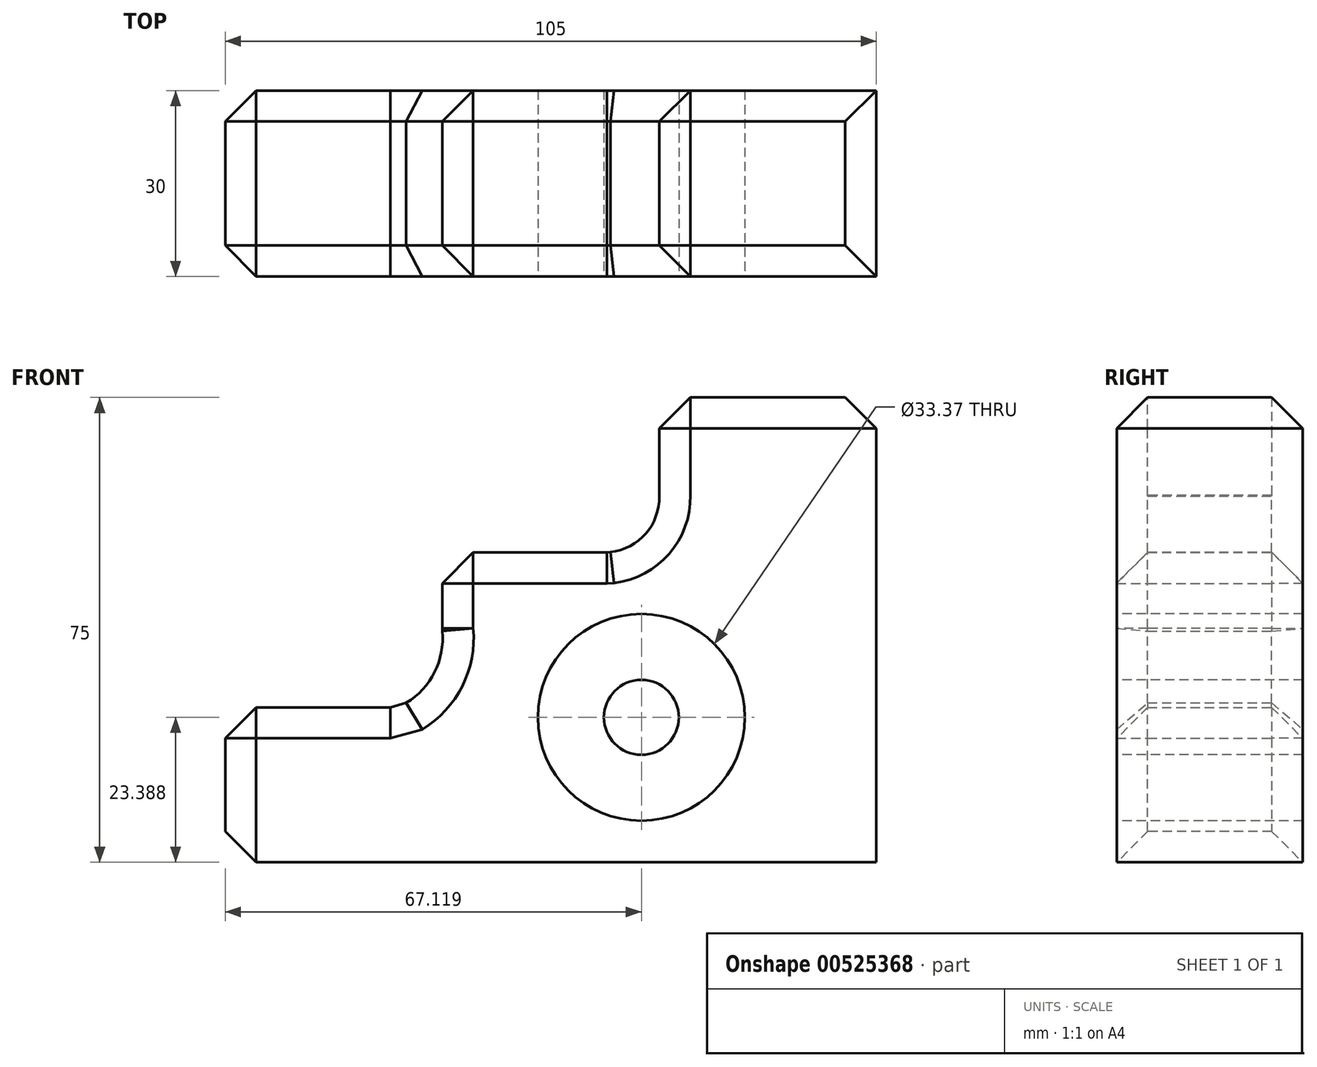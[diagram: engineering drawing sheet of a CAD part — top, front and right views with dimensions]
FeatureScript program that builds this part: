
annotation { "Feature Type Name" : "Feature", "Feature Type Description" : "" }
export const myFeature = defineFeature(function(context is Context, id is Id, definition is map)
    precondition{}
    {
        {
            var Q0;
            Q0=qCreatedBy(makeId("Front.planeOp"),FACE);
            var sketch = newSketch(context, id + "F0", { "sketchPlane" : qUnion([Q0])});
            skLineSegment(sketch, "E0", {"start": v(-61.79, 0) * mm, "end": v(-61.79, 25) * mm});
            skLineSegment(sketch, "E1", {"start": v(-61.79, 25) * mm, "end": v(-26.79, 25) * mm});
            skLineSegment(sketch, "E2", {"start": v(-26.79, 25) * mm, "end": v(-26.79, 50) * mm});
            skLineSegment(sketch, "E3", {"start": v(-26.79, 50) * mm, "end": v(8.21, 50) * mm});
            skLineSegment(sketch, "E4", {"start": v(8.21, 50) * mm, "end": v(8.21, 75) * mm});
            skLineSegment(sketch, "E5", {"start": v(8.21, 75) * mm, "end": v(43.21, 75) * mm});
            skLineSegment(sketch, "E6", {"start": v(43.21, 75) * mm, "end": v(43.21, 0) * mm});
            skLineSegment(sketch, "E7", {"start": v(43.21, 0) * mm, "end": v(-61.79, 0) * mm});
            skArc(sketch, "E8", {"start": v(-33.98, 25) * mm, "mid": v(-28.34, 30.08) * mm, "end": v(-26.79, 37.5) * mm});
            skArc(sketch, "E9", {"start": v(0, 50) * mm, "mid": v(5.95, 52.93) * mm, "end": v(8.21, 59.15) * mm});
            skSolve(sketch);
        }
        {
            var Q0;
            {var subQ12=sQuery(id+"F0.wireOp",EDGE,"E0");Q0=makeQuery(id+"F0.imprint","IMPRINT",FACE,{"disambiguationData":[TD([[makeQuery(id+"F0.imprint","IMPRINT",EDGE,{"derivedFrom":subQ12}),-1.0]])]});}
            var Q1;
            {var subQ0=sQuery(id+"F0.wireOp",EDGE,"E2");var subQ1=sQuery(id+"F0.wireOp",EDGE,"E1");var subQ2=makeQuery(id+"F0.imprint","INTERSECT",VERTEX,{"derivedFrom":[subQ1,subQ0]});Q1=makeQuery(id+"F0.imprint","IMPRINT",FACE,{"disambiguationData":[TD([[makeQuery(id+"F0.imprint","IMPRINT",EDGE,{"disambiguationData":[TD([[subQ2,1.0]])],"derivedFrom":subQ1}),1.0]])]});}
            var Q2;
            {var subQ0=sQuery(id+"F0.wireOp",EDGE,"E4");var subQ1=sQuery(id+"F0.wireOp",EDGE,"E3");var subQ2=makeQuery(id+"F0.imprint","INTERSECT",VERTEX,{"derivedFrom":[subQ1,subQ0]});Q2=makeQuery(id+"F0.imprint","IMPRINT",FACE,{"disambiguationData":[TD([[makeQuery(id+"F0.imprint","IMPRINT",EDGE,{"disambiguationData":[TD([[subQ2,1.0]])],"derivedFrom":subQ1}),1.0]])]});}
            extrude(context, id + "F1", {"entities" : qUnion([Q0, Q1, Q2]), "depth" : 30 * mm, "offsetDistance" : 25 * mm});
        }
        {
            var Q0;
            Q0=makeQuery(id+"F1.opExtrude","CAP_FACE",FACE,{"disambiguationData":[OSD([sQuery(id+"F0.wireOp",EDGE,"E0"),sQuery(id+"F0.wireOp",EDGE,"E1"),sQuery(id+"F0.wireOp",EDGE,"E2"),sQuery(id+"F0.wireOp",EDGE,"E3"),sQuery(id+"F0.wireOp",EDGE,"E4"),sQuery(id+"F0.wireOp",EDGE,"E5"),sQuery(id+"F0.wireOp",EDGE,"E6"),sQuery(id+"F0.wireOp",EDGE,"E7"),sQuery(id+"F0.wireOp",EDGE,"E8"),sQuery(id+"F0.wireOp",EDGE,"E9")])],"isStart":false});
            var sketch = newSketch(context, id + "F2", { "sketchPlane" : qUnion([Q0])});
            skCircle(sketch, "E10", {"center": v(5.33, 23.39) * mm, "radius": 16.69 * mm});
            skCircle(sketch, "E11", {"center": v(5.33, 23.39) * mm, "radius": 6.04 * mm});
            skSolve(sketch);
        }
        {
            var Q0;
            Q0=makeQuery(id+"F2.imprint","IMPRINT",FACE,{"disambiguationData":[TD([[makeQuery(id+"F2.imprint","IMPRINT",EDGE,{"derivedFrom":sQuery(id+"F2.wireOp",EDGE,"E10")}),1.0]])]});
            extrude(context, id + "F3", {"entities" : qUnion([Q0]), "operationType" : NewBodyOperationType.REMOVE, "oppositeDirection" : true, "depth" : 30 * mm, "offsetDistance" : 25 * mm});
        }
        {
            var Q0;
            Q0=makeQuery(id+"F1.opExtrude","SWEPT_EDGE",EDGE,{"disambiguationData":[OSD([sQuery(id+"F0.wireOp",EDGE,"E2"),sQuery(id+"F0.wireOp",EDGE,"E3")])]});
            var Q1;
            Q1=makeQuery(id+"F1.opExtrude","SWEPT_FACE",FACE,{"disambiguationData":[OSD([sQuery(id+"F0.wireOp",EDGE,"E2")])]});
            var Q2;
            Q2=makeQuery(id+"F1.opExtrude","SWEPT_FACE",FACE,{"disambiguationData":[OSD([sQuery(id+"F0.wireOp",EDGE,"E0")])]});
            var Q3;
            Q3=makeQuery(id+"F1.opExtrude","SWEPT_FACE",FACE,{"disambiguationData":[OSD([sQuery(id+"F0.wireOp",EDGE,"E9")])]});
            var Q4;
            Q4=makeQuery(id+"F1.opExtrude","SWEPT_FACE",FACE,{"disambiguationData":[OSD([sQuery(id+"F0.wireOp",EDGE,"E4")])]});
            var Q5;
            Q5=makeQuery(id+"F1.opExtrude","CAP_EDGE",EDGE,{"disambiguationData":[OSD([sQuery(id+"F0.wireOp",EDGE,"E8")])],"isStart":true});
            var Q6;
            Q6=makeQuery(id+"F1.opExtrude","SWEPT_FACE",FACE,{"disambiguationData":[OSD([sQuery(id+"F0.wireOp",EDGE,"E8")])]});
            var Q7;
            Q7=makeQuery(id+"F1.opExtrude","CAP_EDGE",EDGE,{"disambiguationData":[OSD([sQuery(id+"F0.wireOp",EDGE,"E1")])],"isStart":false});
            var Q8;
            Q8=makeQuery(id+"F1.opExtrude","CAP_EDGE",EDGE,{"disambiguationData":[OSD([sQuery(id+"F0.wireOp",EDGE,"E5")])],"isStart":false});
            var Q9;
            Q9=makeQuery(id+"F1.opExtrude","SWEPT_FACE",FACE,{"disambiguationData":[OSD([sQuery(id+"F0.wireOp",EDGE,"E5")])]});
            chamfer(context, id + "F4", {"entities" : qUnion([Q0, Q1, Q2, Q3, Q4, Q5, Q6, Q7, Q8, Q9]), "width" : 5 * mm, "tangentPropagation" : true});
        }
    });
